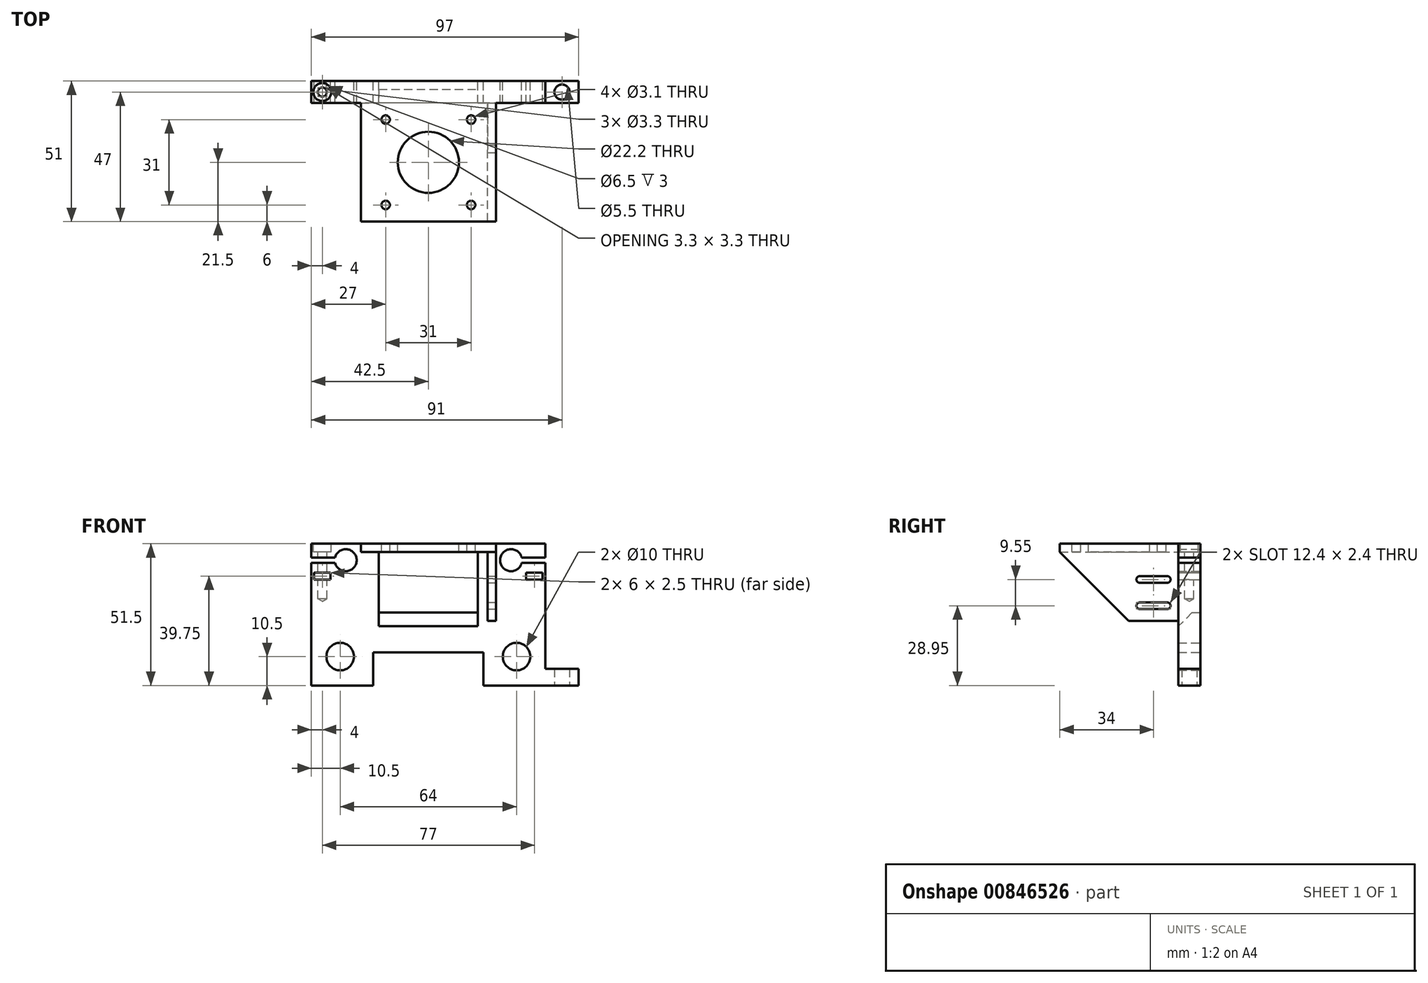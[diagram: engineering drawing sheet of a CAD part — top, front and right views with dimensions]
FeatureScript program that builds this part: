
annotation { "Feature Type Name" : "Feature", "Feature Type Description" : "" }
export const myFeature = defineFeature(function(context is Context, id is Id, definition is map)
    precondition{}
    {
        {
            var Q0;
            Q0=qCreatedBy(makeId("Front.planeOp"),FACE);
            var sketch = newSketch(context, id + "F0", { "sketchPlane" : qUnion([Q0])});
            skLineSegment(sketch, "E0", {"start": v(-42.5, 51.5) * mm, "end": v(-18, 51.5) * mm});
            skLineSegment(sketch, "E1", {"start": v(-18, 51.5) * mm, "end": v(-18, 51.5) * mm});
            skLineSegment(sketch, "E2", {"start": v(-18, 51.5) * mm, "end": v(18, 51.5) * mm});
            skLineSegment(sketch, "E3", {"start": v(18, 51.5) * mm, "end": v(18, 51.5) * mm});
            skLineSegment(sketch, "E4", {"start": v(18, 51.5) * mm, "end": v(42.5, 51.5) * mm});
            skLineSegment(sketch, "E5", {"start": v(42.5, 51.5) * mm, "end": v(42.5, 46.5) * mm});
            skLineSegment(sketch, "E6", {"start": v(42.5, 0) * mm, "end": v(20, 0) * mm});
            skLineSegment(sketch, "E7", {"start": v(20, 0) * mm, "end": v(20, 12) * mm});
            skLineSegment(sketch, "E8", {"start": v(20, 12) * mm, "end": v(-20, 12) * mm});
            skLineSegment(sketch, "E9", {"start": v(-20, 12) * mm, "end": v(-20, 0) * mm});
            skLineSegment(sketch, "E10", {"start": v(-20, 0) * mm, "end": v(-42.5, 0) * mm});
            skLineSegment(sketch, "E11", {"start": v(-42.5, 0) * mm, "end": v(-42.5, 44.5) * mm});
            skArc(sketch, "E12", {"start": v(-33.87, 44.5) * mm, "mid": v(-26, 45.5) * mm, "end": v(-33.87, 46.5) * mm});
            skArc(sketch, "E13", {"start": v(33.87, 46.5) * mm, "mid": v(26, 45.5) * mm, "end": v(33.87, 44.5) * mm});
            skCircle(sketch, "E14", {"center": v(-32, 10.5) * mm, "radius": 5 * mm});
            skCircle(sketch, "E15", {"center": v(32, 10.5) * mm, "radius": 5 * mm});
            skLineSegment(sketch, "E16", {"start": v(-42.5, 46.5) * mm, "end": v(-33.87, 46.5) * mm});
            skLineSegment(sketch, "E17", {"start": v(-33.87, 44.5) * mm, "end": v(-42.5, 44.5) * mm});
            skLineSegment(sketch, "E18", {"start": v(-30, 45.5) * mm, "end": v(-47.26, 45.5) * mm, "construction": true});
            skLineSegment(sketch, "E19.trimOffspring", {"start": v(-42.5, 46.5) * mm, "end": v(-42.5, 51.5) * mm});
            skLineSegment(sketch, "E20.MirrorCS", {"start": v(42.5, 46.5) * mm, "end": v(33.87, 46.5) * mm});
            skLineSegment(sketch, "E21.MirrorCS", {"start": v(33.87, 44.5) * mm, "end": v(42.5, 44.5) * mm});
            skLineSegment(sketch, "E22", {"start": v(-41.5, 41) * mm, "end": v(-35.5, 41) * mm});
            skLineSegment(sketch, "E23", {"start": v(-35.5, 41) * mm, "end": v(-35.5, 38.5) * mm});
            skLineSegment(sketch, "E24", {"start": v(-35.5, 38.5) * mm, "end": v(-41.5, 38.5) * mm});
            skLineSegment(sketch, "E25.trimOffspring", {"start": v(42.5, 44.5) * mm, "end": v(42.5, 0) * mm});
            skLineSegment(sketch, "E26", {"start": v(-38.5, 41) * mm, "end": v(-38.5, 38.5) * mm, "construction": true});
            skLineSegment(sketch, "E27", {"start": v(-41.5, 41) * mm, "end": v(-41.5, 38.5) * mm});
            skLineSegment(sketch, "E28.MirrorCS", {"start": v(35.5, 38.5) * mm, "end": v(41.5, 38.5) * mm});
            skLineSegment(sketch, "E29.MirrorCS", {"start": v(35.5, 41) * mm, "end": v(35.5, 38.5) * mm});
            skLineSegment(sketch, "E30.MirrorCS", {"start": v(41.5, 41) * mm, "end": v(35.5, 41) * mm});
            skLineSegment(sketch, "E31.MirrorCS", {"start": v(41.5, 41) * mm, "end": v(41.5, 38.5) * mm});
            skLineSegment(sketch, "E32.bottom", {"start": v(-18, 48.5) * mm, "end": v(18, 48.5) * mm});
            skLineSegment(sketch, "E32.top", {"start": v(-18, 26.5) * mm, "end": v(18, 26.5) * mm});
            skLineSegment(sketch, "E32.left", {"start": v(-18, 48.5) * mm, "end": v(-18, 26.5) * mm});
            skLineSegment(sketch, "E32.right", {"start": v(18, 48.5) * mm, "end": v(18, 26.5) * mm});
            skSolve(sketch);
        }
        {
            var Q0;
            Q0=qSketchRegion(id+"F0",true);
            extrude(context, id + "F1", {"entities" : qUnion([Q0]), "depth" : 8 * mm, "offsetDistance" : 25 * mm});
        }
        {
            var Q0;
            Q0=makeQuery(id+"F1.opExtrude","CAP_FACE",FACE,{"disambiguationData":[OSD([sQuery(id+"F0.wireOp",EDGE,"E0"),sQuery(id+"F0.wireOp",EDGE,"E1"),sQuery(id+"F0.wireOp",EDGE,"E2"),sQuery(id+"F0.wireOp",EDGE,"E3"),sQuery(id+"F0.wireOp",EDGE,"E4"),sQuery(id+"F0.wireOp",EDGE,"E5"),sQuery(id+"F0.wireOp",EDGE,"E6"),sQuery(id+"F0.wireOp",EDGE,"E7"),sQuery(id+"F0.wireOp",EDGE,"E8"),sQuery(id+"F0.wireOp",EDGE,"E9"),sQuery(id+"F0.wireOp",EDGE,"E10"),sQuery(id+"F0.wireOp",EDGE,"E11"),sQuery(id+"F0.wireOp",EDGE,"E12"),sQuery(id+"F0.wireOp",EDGE,"E13"),sQuery(id+"F0.wireOp",EDGE,"E14"),sQuery(id+"F0.wireOp",EDGE,"E15"),sQuery(id+"F0.wireOp",EDGE,"E16"),sQuery(id+"F0.wireOp",EDGE,"E17"),sQuery(id+"F0.wireOp",EDGE,"E19.trimOffspring"),sQuery(id+"F0.wireOp",EDGE,"E20.MirrorCS"),sQuery(id+"F0.wireOp",EDGE,"E21.MirrorCS"),sQuery(id+"F0.wireOp",EDGE,"90f44b37-8d97-4ec4-bfaf-505aaca20cb3.trimOffspring")])],"isStart":false});
            var sketch = newSketch(context, id + "F2", { "sketchPlane" : qUnion([Q0])});
            skLineSegment(sketch, "E33.0", {"start": v(-22, 51.5) * mm, "end": v(22, 51.5) * mm, "construction": true});
            skLineSegment(sketch, "E34", {"start": v(-24.5, 51.5) * mm, "end": v(-24.5, 48.5) * mm});
            skLineSegment(sketch, "E35", {"start": v(-24.5, 48.5) * mm, "end": v(24.5, 48.5) * mm});
            skLineSegment(sketch, "E36", {"start": v(24.5, 48.5) * mm, "end": v(24.5, 51.5) * mm});
            skLineSegment(sketch, "E37", {"start": v(-24.5, 51.5) * mm, "end": v(24.5, 51.5) * mm});
            skSolve(sketch);
        }
        {
            var Q0;
            Q0=qSketchRegion(id+"F2",true);
            extrude(context, id + "F3", {"entities" : qUnion([Q0]), "operationType" : NewBodyOperationType.ADD, "depth" : 43 * mm, "offsetDistance" : 25 * mm});
        }
        {
            var Q0;
            Q0=makeQuery(id+"F3.boolean.opBoolean","MERGE",FACE,{"derivedFrom":[makeQuery(id+"F1.opExtrude","SWEPT_FACE",FACE,{"disambiguationData":[OSD([sQuery(id+"F0.wireOp",EDGE,"E2")])]}),makeQuery(id+"F3.opExtrude","SWEPT_FACE",FACE,{"disambiguationData":[OSD([sQuery(id+"F2.wireOp",EDGE,"E37")])]})]});
            var sketch = newSketch(context, id + "F4", { "sketchPlane" : qUnion([Q0])});
            skCircle(sketch, "E38", {"center": v(0, -29.5) * mm, "radius": 11.1 * mm});
            skLineSegment(sketch, "E39.bottom", {"start": v(15.5, -14) * mm, "end": v(-15.5, -14) * mm, "construction": true});
            skLineSegment(sketch, "E39.top", {"start": v(15.5, -45) * mm, "end": v(-15.5, -45) * mm, "construction": true});
            skLineSegment(sketch, "E39.left", {"start": v(15.5, -14) * mm, "end": v(15.5, -45) * mm, "construction": true});
            skLineSegment(sketch, "E39.right", {"start": v(-15.5, -14) * mm, "end": v(-15.5, -45) * mm, "construction": true});
            skCircle(sketch, "E40", {"center": v(-15.5, -14) * mm, "radius": 1.55 * mm});
            skCircle(sketch, "E41", {"center": v(15.5, -14) * mm, "radius": 1.55 * mm});
            skCircle(sketch, "E42", {"center": v(15.5, -45) * mm, "radius": 1.55 * mm});
            skCircle(sketch, "E43", {"center": v(-15.5, -45) * mm, "radius": 1.55 * mm});
            skSolve(sketch);
        }
        {
            var Q0;
            Q0=qSketchRegion(id+"F4",true);
            extrude(context, id + "F5", {"entities" : qUnion([Q0]), "operationType" : NewBodyOperationType.REMOVE, "endBound" : BoundingType.UP_TO_NEXT, "oppositeDirection" : true, "depth" : 25 * mm, "offsetDistance" : 25 * mm});
        }
        {
            var Q0;
            Q0=makeQuery(id+"F3.opExtrude","SWEPT_FACE",FACE,{"disambiguationData":[OSD([sQuery(id+"F2.wireOp",EDGE,"E36")])]});
            var sketch = newSketch(context, id + "F6", { "sketchPlane" : qUnion([Q0])});
            skLineSegment(sketch, "E44", {"start": v(-8, 48.5) * mm, "end": v(-51, 48.5) * mm});
            skLineSegment(sketch, "E45", {"start": v(-8, 23.5) * mm, "end": v(-8, 48.5) * mm});
            skLineSegment(sketch, "E46", {"start": v(-8, 23.5) * mm, "end": v(-26, 23.5) * mm});
            skLineSegment(sketch, "E47", {"start": v(-22, 39.7) * mm, "end": v(-12, 39.7) * mm});
            skLineSegment(sketch, "E48", {"start": v(-12, 37.3) * mm, "end": v(-22, 37.3) * mm});
            skArc(sketch, "E49", {"start": v(-12, 37.3) * mm, "mid": v(-10.8, 38.5) * mm, "end": v(-12, 39.7) * mm});
            skLineSegment(sketch, "E50", {"start": v(-8, 33.73) * mm, "end": v(-36.22, 33.73) * mm, "construction": true});
            skLineSegment(sketch, "E51", {"start": v(-12, 38.5) * mm, "end": v(-22, 38.5) * mm, "construction": true});
            skArc(sketch, "E52", {"start": v(-22, 39.7) * mm, "mid": v(-23.2, 38.5) * mm, "end": v(-22, 37.3) * mm});
            skLineSegment(sketch, "E53", {"start": v(-51, 48.5) * mm, "end": v(-26, 23.5) * mm});
            skLineSegment(sketch, "E54.MirrorCS", {"start": v(-22, 27.75) * mm, "end": v(-12, 27.75) * mm});
            skLineSegment(sketch, "E55.MirrorCS", {"start": v(-12, 30.15) * mm, "end": v(-22, 30.15) * mm});
            skArc(sketch, "E56.MirrorCS", {"start": v(-22, 27.75) * mm, "mid": v(-23.2, 28.95) * mm, "end": v(-22, 30.15) * mm});
            skArc(sketch, "E57.MirrorCS", {"start": v(-12, 30.15) * mm, "mid": v(-10.8, 28.95) * mm, "end": v(-12, 27.75) * mm});
            skSolve(sketch);
        }
        {
            var Q0;
            Q0=qSketchRegion(id+"F6",true);
            extrude(context, id + "F7", {"entities" : qUnion([Q0]), "operationType" : NewBodyOperationType.ADD, "oppositeDirection" : true, "depth" : 3 * mm, "offsetDistance" : 25 * mm});
        }
        {
            var Q0;
            Q0=makeQuery(id+"F1.opExtrude","SWEPT_FACE",FACE,{"disambiguationData":[OSD([sQuery(id+"F0.wireOp",EDGE,"E0")])]});
            var sketch = newSketch(context, id + "F8", { "sketchPlane" : qUnion([Q0])});
            skLineSegment(sketch, "E58", {"start": v(-42.5, 0) * mm, "end": v(-42.5, -8) * mm, "construction": true});
            skLineSegment(sketch, "E59", {"start": v(-42.5, -4) * mm, "end": v(-38.5, -4) * mm, "construction": true});
            skSolve(sketch);
        }
        {
            var Q0;
            Q0=sQuery(id+"F8.wireOp",VERTEX,"E59.end");
            var Q1;
            Q1=makeQuery(id+"F1.opExtrude","SWEPT_BODY",BODY,{"disambiguationData":[OSD([sQuery(id+"F0.wireOp",EDGE,"E0"),sQuery(id+"F0.wireOp",EDGE,"E1"),sQuery(id+"F0.wireOp",EDGE,"E2"),sQuery(id+"F0.wireOp",EDGE,"E3"),sQuery(id+"F0.wireOp",EDGE,"E4"),sQuery(id+"F0.wireOp",EDGE,"E5"),sQuery(id+"F0.wireOp",EDGE,"E6"),sQuery(id+"F0.wireOp",EDGE,"E7"),sQuery(id+"F0.wireOp",EDGE,"E8"),sQuery(id+"F0.wireOp",EDGE,"E9"),sQuery(id+"F0.wireOp",EDGE,"E10"),sQuery(id+"F0.wireOp",EDGE,"E11"),sQuery(id+"F0.wireOp",EDGE,"E12"),sQuery(id+"F0.wireOp",EDGE,"E13"),sQuery(id+"F0.wireOp",EDGE,"E14"),sQuery(id+"F0.wireOp",EDGE,"E15"),sQuery(id+"F0.wireOp",EDGE,"E16"),sQuery(id+"F0.wireOp",EDGE,"E17"),sQuery(id+"F0.wireOp",EDGE,"E19.trimOffspring"),sQuery(id+"F0.wireOp",EDGE,"E20.MirrorCS"),sQuery(id+"F0.wireOp",EDGE,"E21.MirrorCS"),sQuery(id+"F0.wireOp",EDGE,"90f44b37-8d97-4ec4-bfaf-505aaca20cb3.trimOffspring")])]});
            hole(context, id + "F9", {"style" : HoleStyle.C_BORE, "endStyle" : HoleEndStyle.BLIND, "standardTappedOrClearance" : lookupTablePath({ "standard" : "ISO", "fit" : "Normal", "size" : "M3", "type" : "Clearance" }), "standardBlindInLast" : lookupTablePath({ "fit" : "Standard", "standard" : "ISO", "size" : "M3", "type" : "Clearance" }), "holeDiameter" : 3.3 * mm, "cBoreDiameter" : 6.5 * mm, "cBoreDepth" : 3 * mm, "majorDiameter" : 5 * mm, "holeDepth" : 20 * mm, "isTappedThrough" : true, "tappedDepth" : 12 * mm, "tapClearance" : 3, "locations" : qUnion([Q0]), "scope" : qUnion([Q1])});
        }
        {
            var Q0;
            Q0=makeQuery(id+"F1.opExtrude","SWEPT_FACE",FACE,{"disambiguationData":[OSD([sQuery(id+"F0.wireOp",EDGE,"E6")])]});
            var sketch = newSketch(context, id + "F10", { "sketchPlane" : qUnion([Q0])});
            skLineSegment(sketch, "E60.0", {"start": v(42.5, 8) * mm, "end": v(42.5, 0) * mm});
            skLineSegment(sketch, "E61", {"start": v(42.5, 8) * mm, "end": v(54.5, 8) * mm});
            skLineSegment(sketch, "E62", {"start": v(54.5, 8) * mm, "end": v(54.5, 0) * mm});
            skLineSegment(sketch, "E63", {"start": v(54.5, 0) * mm, "end": v(42.5, 0) * mm});
            skLineSegment(sketch, "E64", {"start": v(42.5, 4) * mm, "end": v(54.5, 4) * mm, "construction": true});
            skPoint(sketch, "E65", {"position": v(48.5, 4) * mm});
            skCircle(sketch, "E66", {"center": v(48.5, 4) * mm, "radius": 2.75 * mm});
            skSolve(sketch);
        }
        {
            var Q0;
            Q0=qSketchRegion(id+"F10",true);
            extrude(context, id + "F11", {"entities" : qUnion([Q0]), "operationType" : NewBodyOperationType.ADD, "oppositeDirection" : true, "depth" : 6 * mm, "offsetDistance" : 25 * mm});
        }
        {
            var Q0;
            Q0=makeQuery(id+"F1.opExtrude","CAP_EDGE",EDGE,{"disambiguationData":[OSD([sQuery(id+"F0.wireOp",EDGE,"E32.top")])],"isStart":false});
            chamfer(context, id + "F12", {"entities" : qUnion([Q0]), "width" : 5 * mm, "tangentPropagation" : true});
        }
    });
